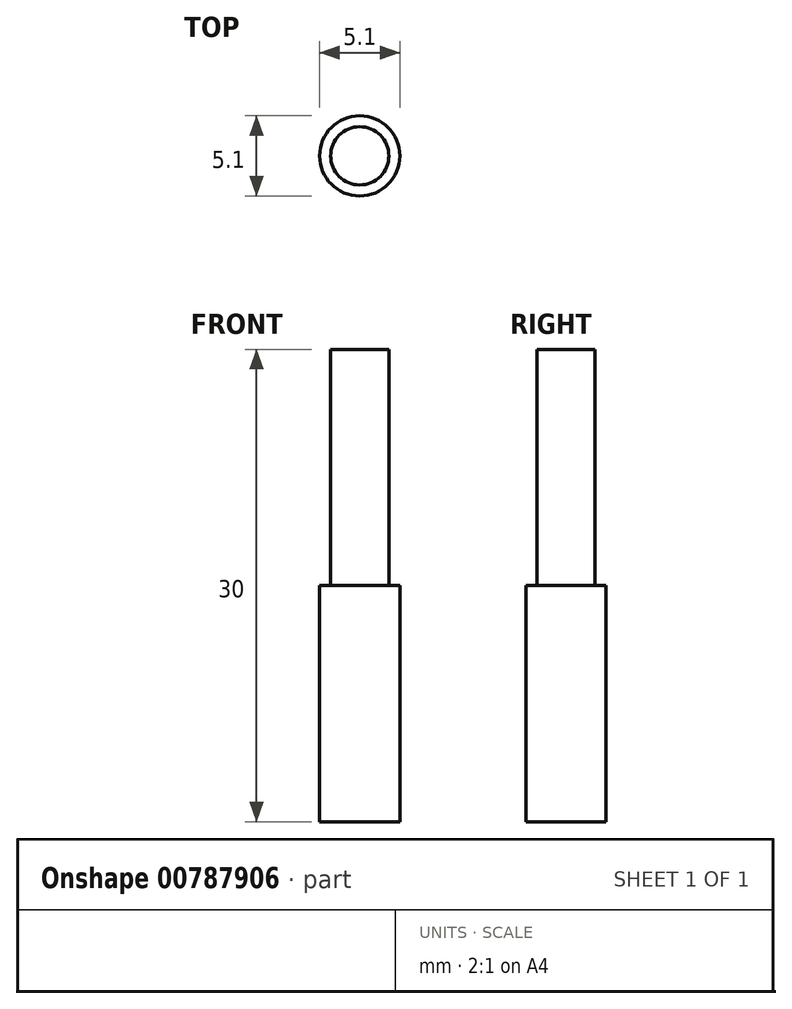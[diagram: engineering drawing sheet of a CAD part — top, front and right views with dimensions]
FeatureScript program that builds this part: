
annotation { "Feature Type Name" : "Feature", "Feature Type Description" : "" }
export const myFeature = defineFeature(function(context is Context, id is Id, definition is map)
    precondition{}
    {
        {
            var Q0;
            Q0=qCreatedBy(makeId("Top.planeOp"),FACE);
            var sketch = newSketch(context, id + "F0", { "sketchPlane" : qUnion([Q0])});
            skCircle(sketch, "E0", {"center": v(0, 0) * mm, "radius": 2.55 * mm});
            skSolve(sketch);
        }
        {
            var Q0;
            Q0=makeQuery(id+"F0.imprint","IMPRINT",FACE,{"disambiguationData":[TD([[makeQuery(id+"F0.imprint","IMPRINT",EDGE,{"derivedFrom":sQuery(id+"F0.wireOp",EDGE,"E0")}),1.0]])]});
            extrude(context, id + "F1", {"entities" : qUnion([Q0]), "depth" : 15 * mm, "offsetDistance" : 25 * mm});
        }
        {
            var Q0;
            Q0=makeQuery(id+"F1.opExtrude","CAP_FACE",FACE,{"disambiguationData":[OSD([sQuery(id+"F0.wireOp",EDGE,"E0")])],"isStart":false});
            var sketch = newSketch(context, id + "F2", { "sketchPlane" : qUnion([Q0])});
            skCircle(sketch, "E1", {"center": v(0, 0) * mm, "radius": 1.85 * mm});
            skSolve(sketch);
        }
        {
            var Q0;
            Q0=qSketchRegion(id+"F2",true);
            extrude(context, id + "F3", {"entities" : qUnion([Q0]), "operationType" : NewBodyOperationType.ADD, "depth" : 15 * mm, "offsetDistance" : 25 * mm});
        }
    });
